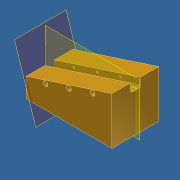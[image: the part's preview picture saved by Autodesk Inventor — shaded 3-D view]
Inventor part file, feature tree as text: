
AUTODESK INVENTOR PART (.ipt)
format: ipt  version: unknown  size: 217,088 bytes
history: native  units: in
note: dims shown in document units (in); Inventor stores cm internally (conversion verified against a paired STEP export)
features: sketch x3, extrude x2, plane x1, hole x1, mirror x1
ambient origin geometry x8: Origin, YZ Plane, XZ Plane, XY Plane, X Axis, Y Axis, Z Axis, Center Point
bodies: Solid1 (feature_tree)
feature tree (8):
  extrude  "Extrusion1"  Depth=2.75in
  plane  "Work Plane1"
  extrude  "Extrusion2"  Depth=0.625in
  hole  "Hole1"  [1 undecoded]
  mirror  "Mirror1"
  sketch  "Sketch1"  dims[d0=0.1237in d1=2.75in]
  sketch  "Sketch2"  dims[d2=1.375in d3=0.625in]
  sketch  "Sketch3"  dims[d4=1.5in d5=0.0in d6=0.1237in d7=0.3125in d8=0.1562in d9=0.2656in d10=0.0625in d11=1.5in d12=0.0in d16=0.0in d19=0.067in d20=0.625in d21=0.156in d22=0.375in d23=0.5635in d24=0.75in d25=0.8108in d29=0.625in d30=0.625in d31=0.0938in]
note: 1 required parameter value undecoded (feature->parameter linkage not recoverable at this tier; creation-order binding heuristic only, values carry confidence <= 0.55)
